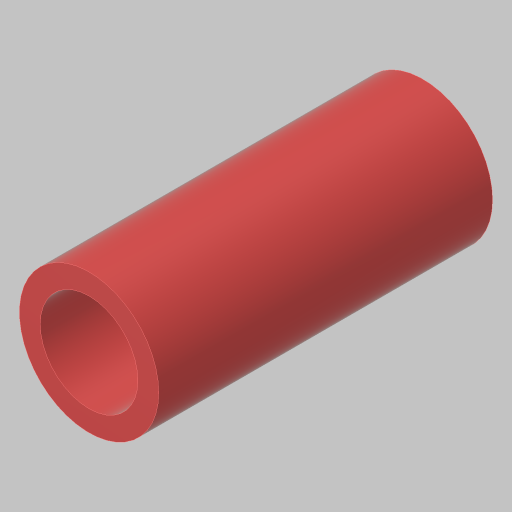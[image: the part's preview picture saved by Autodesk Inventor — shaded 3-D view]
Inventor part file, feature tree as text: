
AUTODESK INVENTOR PART (.ipt)
format: ipt  version: 2023.5 (Build 275446000, 446)  size: 111,104 bytes
history: native  units: in
note: dims shown in document units (in); Inventor stores cm internally (conversion verified against a paired STEP export)
features: extrude x1, sketch x1
ambient origin geometry x8: Origin, YZ Plane, XZ Plane, XY Plane, X Axis, Y Axis, Z Axis, Center Point
bodies: Solid1 (feature_tree)
feature tree (2):
  extrude  "Extrusion1"  Depth=2.0in
  sketch  "Sketch1"  dims[d0=0.585in d1=0.125in d2=2.0in d3=0.0in]
